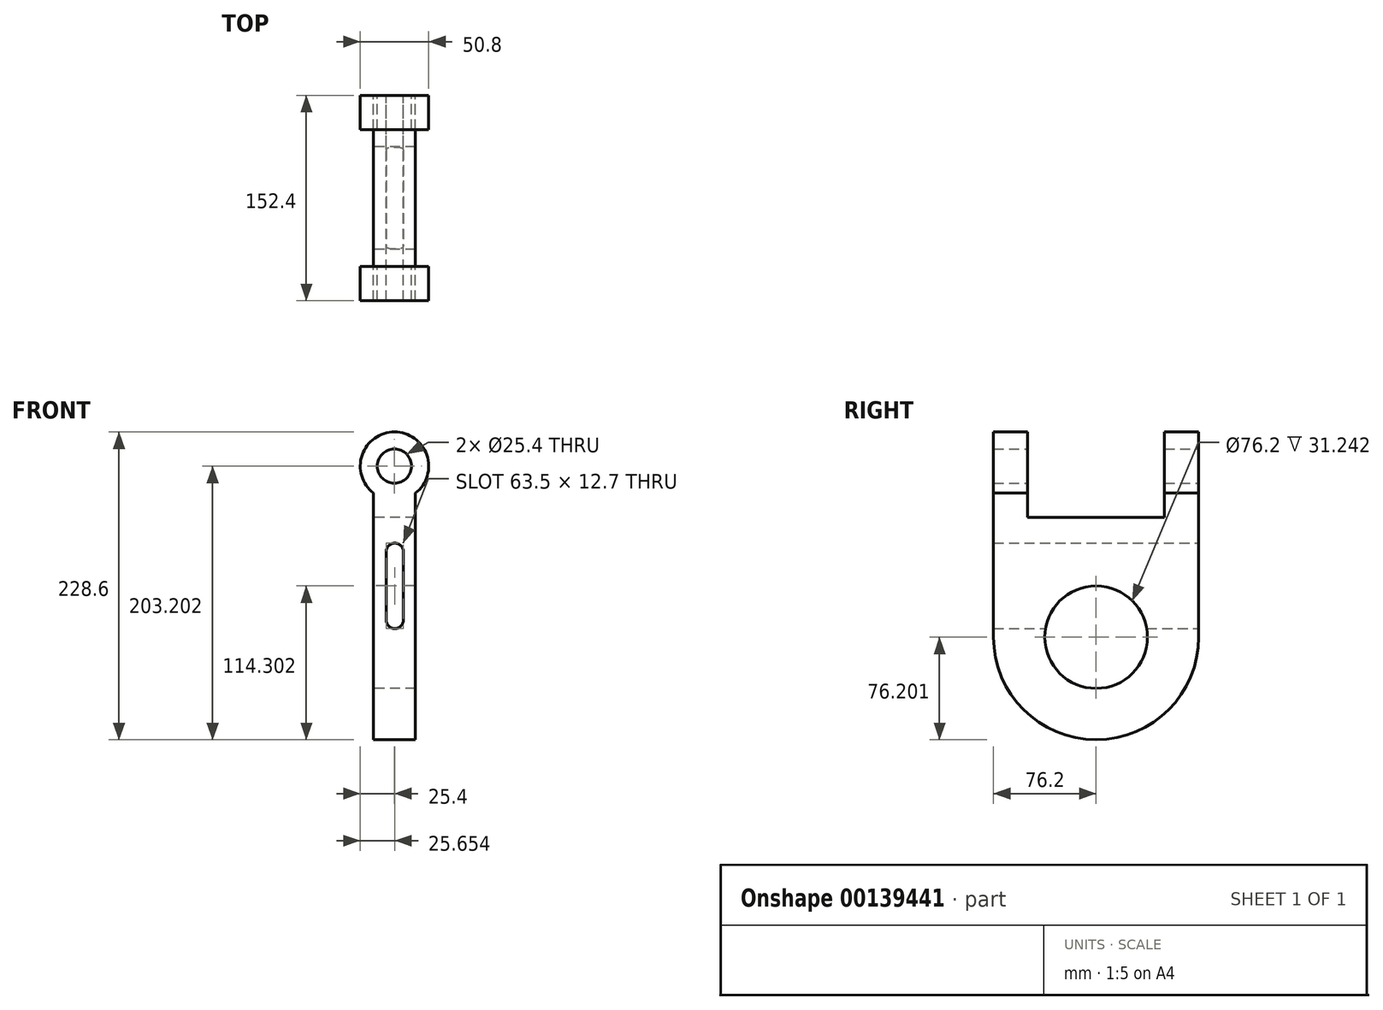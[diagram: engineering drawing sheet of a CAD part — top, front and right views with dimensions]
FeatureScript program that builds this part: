
annotation { "Feature Type Name" : "Feature", "Feature Type Description" : "" }
export const myFeature = defineFeature(function(context is Context, id is Id, definition is map)
    precondition{}
    {
        {
            var Q0;
            Q0=qCreatedBy(makeId("Front.planeOp"),FACE);
            var sketch = newSketch(context, id + "F0", { "sketchPlane" : qUnion([Q0])});
            skCircle(sketch, "E0", {"center": v(0, 38.3) * mm, "radius": 25.4 * mm});
            skCircle(sketch, "E1", {"center": v(0, 38.3) * mm, "radius": 12.7 * mm});
            skLineSegment(sketch, "E2", {"start": v(-15.62, 18.26) * mm, "end": v(-15.62, -164.9) * mm});
            skLineSegment(sketch, "E3", {"start": v(15.62, 18.26) * mm, "end": v(15.62, -164.9) * mm});
            skLineSegment(sketch, "E4", {"start": v(-15.62, -164.9) * mm, "end": v(15.62, -164.9) * mm});
            skSolve(sketch);
        }
        {
            var Q0;
            Q0 = qSketchRegion(id + "F0", true);
            extrude(context, id + "F1", {"entities" : qUnion([Q0]), "depth" : 152.4 * mm});
        }
        {
            var Q0;
            Q0=makeQuery(id+"F1.opExtrude","CAP_EDGE",EDGE,{"disambiguationData":[OSD([sQuery(id+"F0.wireOp",EDGE,"wTOGCP4L-74JC-A4kW-V8jI-FRKfjIFqXPb9")])],"isStart":false});
            var Q1;
            Q1=makeQuery(id+"F1.opExtrude","CAP_EDGE",EDGE,{"disambiguationData":[OSD([sQuery(id+"F0.wireOp",EDGE,"wTOGCP4L-74JC-A4kW-V8jI-FRKfjIFqXPb9")])],"isStart":true});
            var Q2;
            Q2=makeQuery(id+"F1.opExtrude","CAP_EDGE",EDGE,{"disambiguationData":[OSD([sQuery(id+"F0.wireOp",EDGE,"E4")])],"isStart":false});
            var Q3;
            Q3=makeQuery(id+"F1.opExtrude","CAP_EDGE",EDGE,{"disambiguationData":[OSD([sQuery(id+"F0.wireOp",EDGE,"E4")])],"isStart":true});
            fillet(context, id + "F2", {"entities" : qUnion([Q0, Q1, Q2, Q3]), "radius" : 76.2 * mm, "tangentPropagation" : true, "allowEdgeOverflow" : false});
        }
        {
            var Q0;
            Q0=makeQuery(id+"F1.opExtrude","SWEPT_FACE",FACE,{"disambiguationData":[OSD([sQuery(id+"F0.wireOp",EDGE,"E2")])]});
            var sketch = newSketch(context, id + "F3", { "sketchPlane" : qUnion([Q0])});
            skLineSegment(sketch, "E5", {"start": v(25.4, 18.26) * mm, "end": v(127, 18.26) * mm});
            skLineSegment(sketch, "E6", {"start": v(25.4, 18.26) * mm, "end": v(25.4, 74.92) * mm});
            skLineSegment(sketch, "E7", {"start": v(25.4, 74.92) * mm, "end": v(127, 74.92) * mm});
            skLineSegment(sketch, "E8", {"start": v(127, 74.92) * mm, "end": v(127, 18.26) * mm});
            skLineSegment(sketch, "E9", {"start": v(25.4, 18.26) * mm, "end": v(25.4, 0.2) * mm});
            skLineSegment(sketch, "E10", {"start": v(25.4, 0.2) * mm, "end": v(127, 0.2) * mm});
            skLineSegment(sketch, "E11", {"start": v(127, 0.2) * mm, "end": v(127, 18.26) * mm});
            skCircle(sketch, "E12", {"center": v(76.2, -88.7) * mm, "radius": 38.1 * mm});
            skSolve(sketch);
        }
        {
            var Q0;
            Q0=makeQuery(id+"F3.imprint","IMPRINT",FACE,{"disambiguationData":[TD([[makeQuery(id+"F3.imprint","IMPRINT",EDGE,{"derivedFrom":sQuery(id+"F3.wireOp",EDGE,"E5")}),-1.0]])]});
            extrude(context, id + "F4", {"entities" : qUnion([Q0]), "operationType" : NewBodyOperationType.REMOVE, "endBound" : BoundingType.THROUGH_ALL, "oppositeDirection" : true, "depth" : 25.4 * mm, "hasSecondDirection" : true, "secondDirectionOppositeDirection" : false, "secondDirectionDepth" : 25.4 * mm});
        }
        {
            var Q0;
            Q0=qCreatedBy(makeId("Front.planeOp"),FACE);
            var sketch = newSketch(context, id + "F5", { "sketchPlane" : qUnion([Q0])});
            skLineSegment(sketch, "E13", {"start": v(-6.1, -25.2) * mm, "end": v(-6.1, -76) * mm});
            skLineSegment(sketch, "E14", {"start": v(6.6, -25.2) * mm, "end": v(6.6, -76) * mm});
            skArc(sketch, "E15", {"start": v(-6.1, -25.2) * mm, "mid": v(0.25, -18.86) * mm, "end": v(6.6, -25.2) * mm});
            skArc(sketch, "E16", {"start": v(-6.1, -76) * mm, "mid": v(0.25, -82.36) * mm, "end": v(6.6, -76) * mm});
            skSolve(sketch);
        }
        {
            var Q0;
            Q0 = qSketchRegion(id + "F5", true);
            extrude(context, id + "F6", {"entities" : qUnion([Q0]), "operationType" : NewBodyOperationType.REMOVE, "endBound" : BoundingType.THROUGH_ALL, "depth" : 25.4 * mm});
        }
        {
            var Q0;
            Q0=makeQuery(id+"F3.imprint","IMPRINT",FACE,{"disambiguationData":[TD([[makeQuery(id+"F3.imprint","IMPRINT",EDGE,{"derivedFrom":sQuery(id+"F3.wireOp",EDGE,"E5")}),1.0]])]});
            extrude(context, id + "F7", {"entities" : qUnion([Q0]), "operationType" : NewBodyOperationType.REMOVE, "endBound" : BoundingType.THROUGH_ALL, "oppositeDirection" : true, "depth" : 25.4 * mm});
        }
        {
            var Q0;
            Q0=makeQuery(id+"F3.imprint","IMPRINT",FACE,{"disambiguationData":[TD([[makeQuery(id+"F3.imprint","IMPRINT",EDGE,{"derivedFrom":sQuery(id+"F3.wireOp",EDGE,"E12")}),1.0]])]});
            extrude(context, id + "F8", {"entities" : qUnion([Q0]), "operationType" : NewBodyOperationType.REMOVE, "endBound" : BoundingType.THROUGH_ALL, "oppositeDirection" : true, "depth" : 25.4 * mm});
        }
    });
